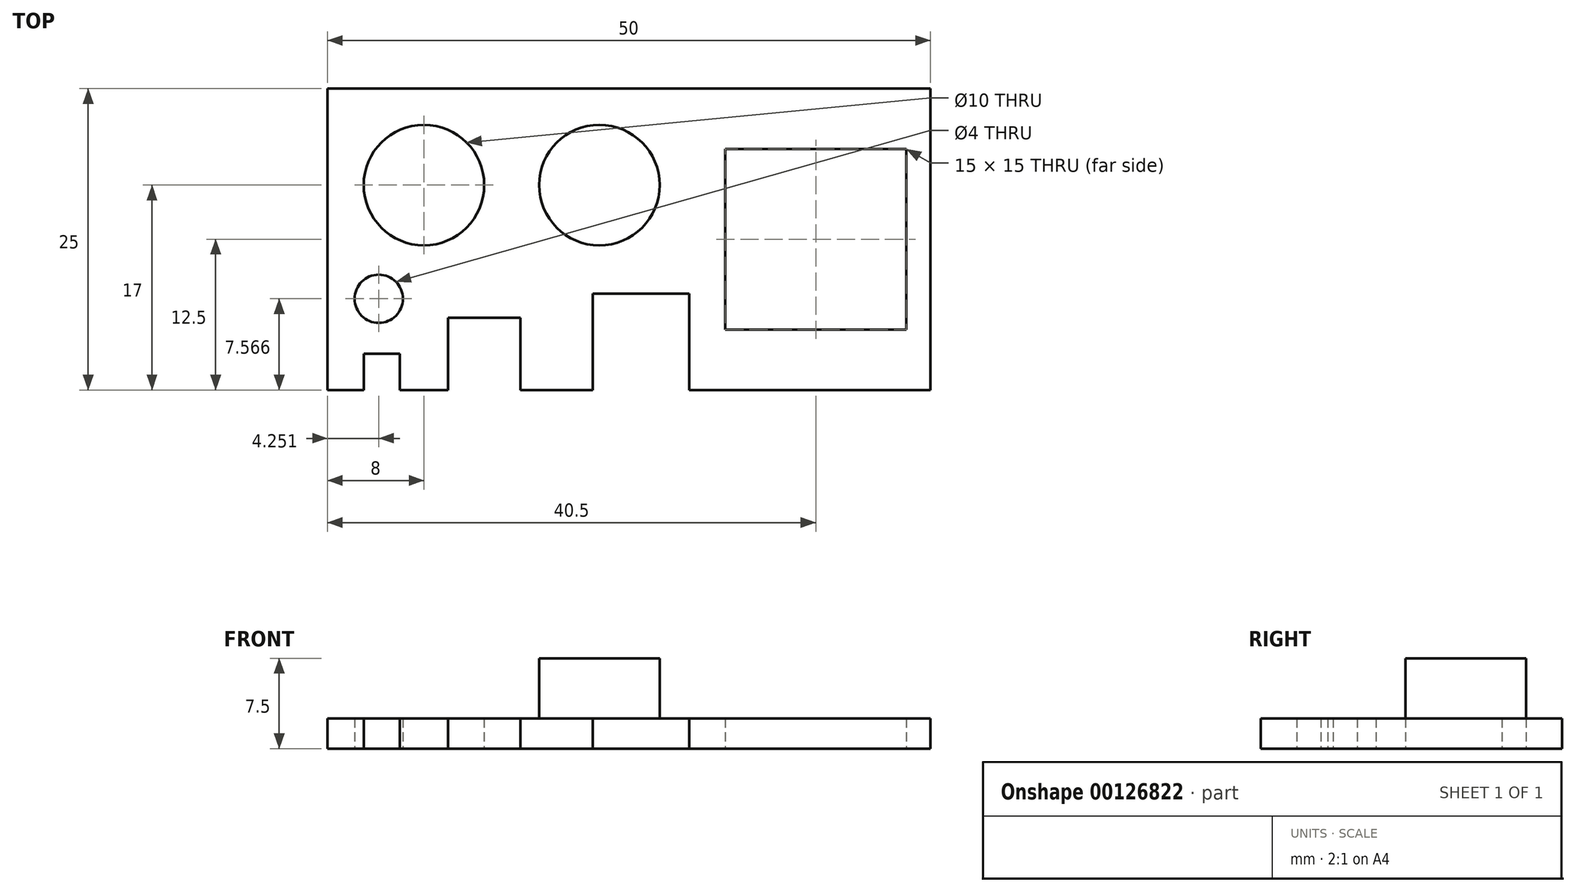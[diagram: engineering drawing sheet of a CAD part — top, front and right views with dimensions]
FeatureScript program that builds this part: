
annotation { "Feature Type Name" : "Feature", "Feature Type Description" : "" }
export const myFeature = defineFeature(function(context is Context, id is Id, definition is map)
    precondition{}
    {
        {
            var Q0;
            Q0=qCreatedBy(makeId("Top.planeOp"),FACE);
            var sketch = newSketch(context, id + "F0", { "sketchPlane" : qUnion([Q0])});
            skLineSegment(sketch, "E0.bottom", {"start": v(0, 0) * mm, "end": v(3, 0) * mm});
            skLineSegment(sketch, "E0.top", {"start": v(0, 25) * mm, "end": v(50, 25) * mm});
            skLineSegment(sketch, "E0.left", {"start": v(0, 0) * mm, "end": v(0, 25) * mm});
            skLineSegment(sketch, "E0.right", {"start": v(50, 0) * mm, "end": v(50, 25) * mm});
            skCircle(sketch, "E1", {"center": v(8, 17) * mm, "radius": 5 * mm});
            skLineSegment(sketch, "E2.bottom", {"start": v(33, 20) * mm, "end": v(48, 20) * mm});
            skLineSegment(sketch, "E2.top", {"start": v(33, 5) * mm, "end": v(48, 5) * mm});
            skLineSegment(sketch, "E2.left", {"start": v(33, 20) * mm, "end": v(33, 5) * mm});
            skLineSegment(sketch, "E2.right", {"start": v(48, 20) * mm, "end": v(48, 5) * mm});
            skLineSegment(sketch, "E3.top", {"start": v(3, 3) * mm, "end": v(6, 3) * mm});
            skLineSegment(sketch, "E3.left", {"start": v(3, 0) * mm, "end": v(3, 3) * mm});
            skLineSegment(sketch, "E3.right", {"start": v(6, 0) * mm, "end": v(6, 3) * mm});
            skLineSegment(sketch, "E4.top", {"start": v(10, 6) * mm, "end": v(16, 6) * mm});
            skLineSegment(sketch, "E4.left", {"start": v(10, 0) * mm, "end": v(10, 6) * mm});
            skLineSegment(sketch, "E4.right", {"start": v(16, 0) * mm, "end": v(16, 6) * mm});
            skLineSegment(sketch, "E5.top", {"start": v(22, 8) * mm, "end": v(30, 8) * mm});
            skLineSegment(sketch, "E5.left", {"start": v(22, 0) * mm, "end": v(22, 8) * mm});
            skLineSegment(sketch, "E5.right", {"start": v(30, 0) * mm, "end": v(30, 8) * mm});
            skLineSegment(sketch, "E6.trimOffspring", {"start": v(6, 0) * mm, "end": v(10, 0) * mm});
            skLineSegment(sketch, "E7.trimOffspring", {"start": v(16, 0) * mm, "end": v(22, 0) * mm});
            skLineSegment(sketch, "E8.trimOffspring", {"start": v(30, 0) * mm, "end": v(50, 0) * mm});
            skCircle(sketch, "E9", {"center": v(4.25, 7.57) * mm, "radius": 2 * mm});
            skSolve(sketch);
        }
        {
            var Q0;
            Q0=makeQuery(id+"F0.imprint","IMPRINT",FACE,{"disambiguationData":[TD([[makeQuery(id+"F0.imprint","IMPRINT",EDGE,{"derivedFrom":sQuery(id+"F0.wireOp",EDGE,"E0.bottom")}),1.0]])]});
            extrude(context, id + "F1", {"entities" : qUnion([Q0]), "depth" : 2.5 * mm});
        }
        {
            var Q0;
            Q0=makeQuery(id+"F1.opExtrude","CAP_FACE",FACE,{"disambiguationData":[OSD([sQuery(id+"F0.wireOp",EDGE,"E0.bottom"),sQuery(id+"F0.wireOp",EDGE,"E0.top"),sQuery(id+"F0.wireOp",EDGE,"E0.left"),sQuery(id+"F0.wireOp",EDGE,"E0.right"),sQuery(id+"F0.wireOp",EDGE,"E1"),sQuery(id+"F0.wireOp",EDGE,"E2.bottom"),sQuery(id+"F0.wireOp",EDGE,"E2.top"),sQuery(id+"F0.wireOp",EDGE,"E2.left"),sQuery(id+"F0.wireOp",EDGE,"E2.right"),sQuery(id+"F0.wireOp",EDGE,"E3.top"),sQuery(id+"F0.wireOp",EDGE,"E3.left"),sQuery(id+"F0.wireOp",EDGE,"E3.right"),sQuery(id+"F0.wireOp",EDGE,"E4.top"),sQuery(id+"F0.wireOp",EDGE,"E4.left"),sQuery(id+"F0.wireOp",EDGE,"E4.right"),sQuery(id+"F0.wireOp",EDGE,"E5.top"),sQuery(id+"F0.wireOp",EDGE,"E5.left"),sQuery(id+"F0.wireOp",EDGE,"E5.right"),sQuery(id+"F0.wireOp",EDGE,"E6.trimOffspring"),sQuery(id+"F0.wireOp",EDGE,"E7.trimOffspring"),sQuery(id+"F0.wireOp",EDGE,"E8.trimOffspring")])],"isStart":false});
            var sketch = newSketch(context, id + "F2", { "sketchPlane" : qUnion([Q0])});
            skCircle(sketch, "E10", {"center": v(22.55, 17) * mm, "radius": 5 * mm});
            skSolve(sketch);
        }
        {
            var Q0;
            Q0=makeQuery(id+"F2.imprint","IMPRINT",FACE,{"disambiguationData":[TD([[makeQuery(id+"F2.imprint","IMPRINT",EDGE,{"derivedFrom":sQuery(id+"F2.wireOp",EDGE,"E10")}),1.0]])]});
            extrude(context, id + "F3", {"entities" : qUnion([Q0]), "operationType" : NewBodyOperationType.ADD, "depth" : 5 * mm});
        }
    });
